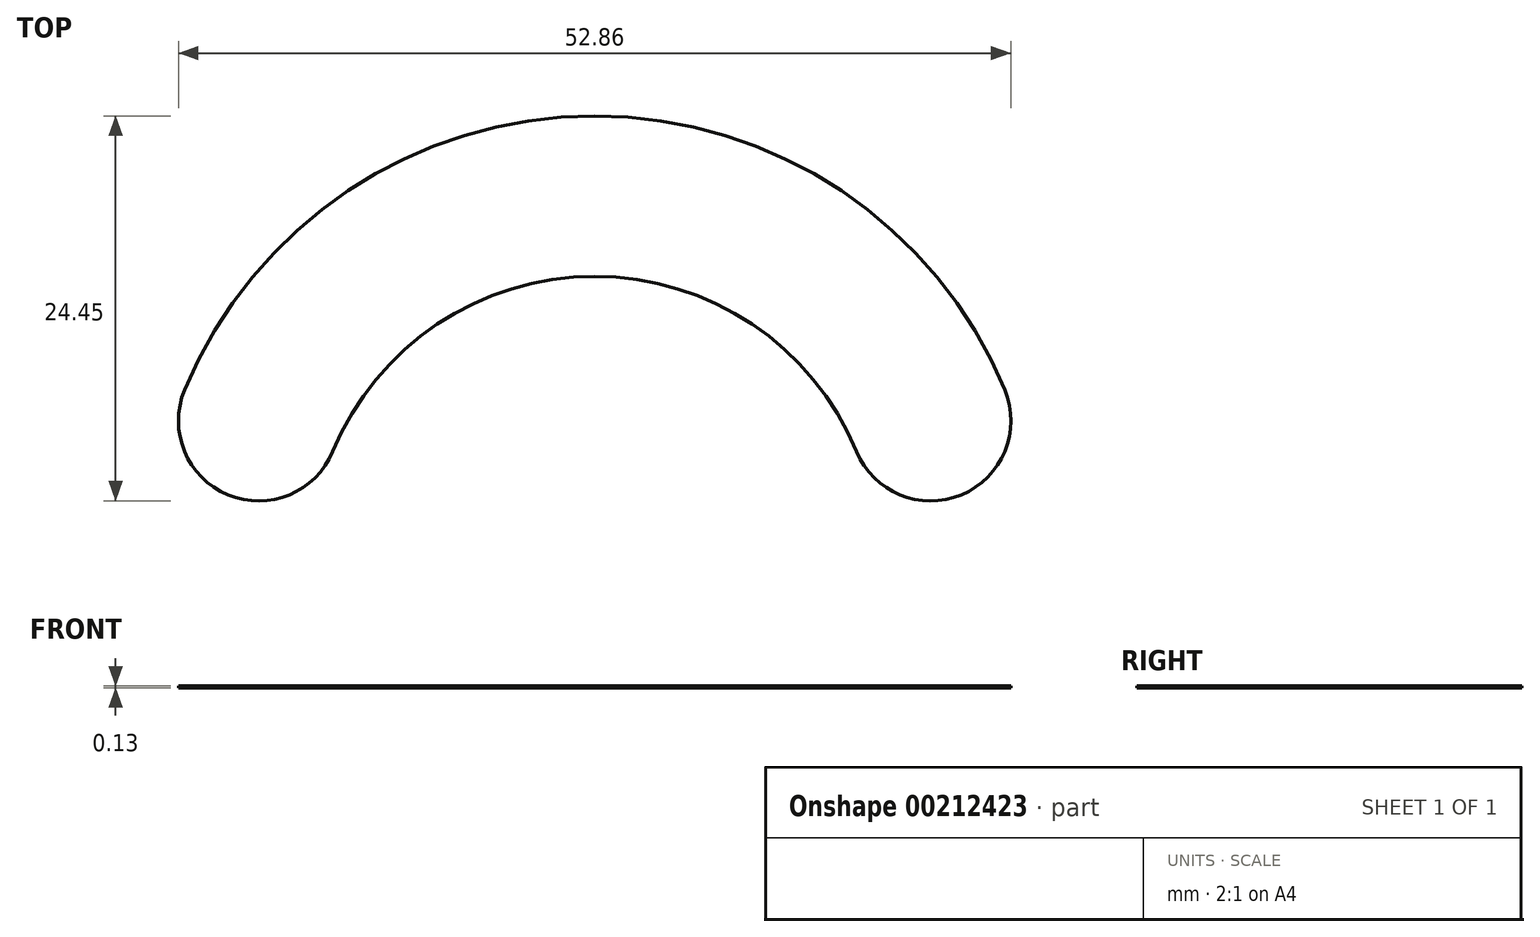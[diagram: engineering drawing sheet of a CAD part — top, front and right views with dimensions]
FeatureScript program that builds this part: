
annotation { "Feature Type Name" : "Feature", "Feature Type Description" : "" }
export const myFeature = defineFeature(function(context is Context, id is Id, definition is map)
    precondition{}
    {
        {
            var Q0;
            Q0=qCreatedBy(makeId("Top.planeOp"),FACE);
            var sketch = newSketch(context, id + "F0", { "sketchPlane" : qUnion([Q0])});
            skLineSegment(sketch, "E0", {"start": v(0, 0) * mm, "end": v(-21.34, 8.84) * mm, "construction": true});
            skLineSegment(sketch, "E1", {"start": v(0, 0) * mm, "end": v(21.34, 8.84) * mm, "construction": true});
            skArc(sketch, "E2", {"start": v(26.05, 10.79) * mm, "mid": v(0, 28.2) * mm, "end": v(-26.05, 10.79) * mm});
            skArc(sketch, "E3", {"start": v(16.63, 6.89) * mm, "mid": v(0, 18) * mm, "end": v(-16.63, 6.89) * mm});
            skArc(sketch, "E4", {"start": v(-26.05, 10.79) * mm, "mid": v(-23.29, 4.13) * mm, "end": v(-16.63, 6.89) * mm});
            skArc(sketch, "E5", {"start": v(16.63, 6.89) * mm, "mid": v(23.29, 4.13) * mm, "end": v(26.05, 10.79) * mm});
            skSolve(sketch);
        }
        {
            var Q0;
            Q0=makeQuery(id+"F0.imprint","IMPRINT",FACE,{"disambiguationData":[TD([[makeQuery(id+"F0.imprint","IMPRINT",EDGE,{"derivedFrom":sQuery(id+"F0.wireOp",EDGE,"E2")}),1.0]])]});
            extrude(context, id + "F1", {"entities" : qUnion([Q0]), "depth" : 0.13 * mm});
        }
    });
